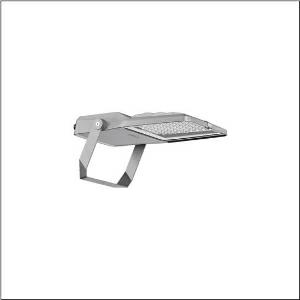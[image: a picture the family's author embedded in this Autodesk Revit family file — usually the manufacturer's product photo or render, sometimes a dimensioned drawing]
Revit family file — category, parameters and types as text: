
# Revit family: floodlight_fl_21_iq_mini___pl52_5xa7772c4d1a_fae4
name_source: partatom
category: Lighting Fixtures
units: mm (PartAtom-declared; Revit-internal decimal feet)

## family parameters
Cut with Voids When Loaded = No
Host = Face
Light Source = No
Part Type = Normal
Room Calculation Point = No
Round Connector Dimension = Use Diameter
Shared = No

## types (1)
- --- (1 x LED, 12720 lm, 87.2 W, 4000K)
    Apparent Load = 87 VA
    CIE Flux Codes = 26 60 98 100 100
    Color Rendering = 70
    Color Temperature = 4000K
    Default Elevation = 1800 mm
    Description = Floodlight FL 21 iQ mini, floodlight, primary light control with lens, of PMMA, primary optical cover: protective disc, of toughened safety glass, transparent, light distribution: PL52, light emission: direct distribution, installation type: surface-mounted, lamps: LED, High Power LED, rated values: 12.720lm | 87,2W | 145,9lm/W (begin service life); end service life: 12.720lm | 92,1W; at 50% lumin. flux: 6.360lm | 40,2W | 158,2lm/W, colour temperature: 4000K, colour rendering: CRI > 70, light colour: 740, light setting 1 begin service life: 100% | 12.720lm | 87,2W | 145,9lm/W | 4.000K, light setting 1 end service life: 92,1W, further light settings possible, control: Street-Remote, Auto-Match, Temp-Guard, Night-Set, Smart-Wire, Desk-Remote (wireless, voltage-free reading and setting of iQ features in the workshop via application-optimized NFC function/RFID function), optimised constant luminous flux control (CLO 2.0), pre-setting: linear dimming characteristic, with terminal, 6-pole, mains connection: 220..240V, AC, 50/60Hz, luminaire housing, of diecast aluminium, powder-coated, SITECO metallic grey (DB 702S), corrosivity category C5 mid according to DIN EN ISO 12944suitable for swimming poolschlorine-resistant, sealing non-destructively replaceable, mounting bracket, of steel, galvanised, powder-coated, SITECO metallic grey (DB 702S), protection rating (complete): IP66, insulation class (complete): insulation class II (safety insulation), certification: CE, ENEC, VDE, protection symbol: D, impact resistance: IK08, permissible operating ambient temperature: -40..+40°C, permissible operating ambient temperature for outdoor applications: -40..+50°C, standard: DIN EN 12944, LABS conformity tested according to VDMA 24364:2018-05, packaging unit: 1 piece

Light Distribution: PL52
    Height = 70 mm
    Lamp = 1 x LED
    Lamp Light Flux = 12720 lm
    Lamp Power = 87.2 W
    Lamp count = 1
    Length = 485 mm
    Luminous efficacy = 146 lm/W
    Manufacturer = Siteco
    ModVariant = No
    Model = 5XA7772C4D1A
    Number of Poles = 1
    OnlyDefault = Yes
    Power Factor = 1
    Product Name = Floodlight FL 21 iQ mini | PL52
    Product group = floodlight | pylon annexe
    ProductGroupID = 6201
    Protection Class = Protection class II
    Protection Degree = IP 66
    RLX_Detail_Level = 1
    RLX_Emergency_Light_Flux = 0 lm
    RLX_Emergency_Type = 0
    RLX_Emergency_Type_DB = No
    RlxData = <blob elided: 96805 chars, md5=f06a925e>
    Socket = socket
    Standby Power = 0 W
    System Light Flux = 12720 lm
    System Power = 87 W
    Type Comments = factory setting: luminous flux: 100 % | dim-lin: 254 | 456 mA
    Type Image = l_1006845.jpg
    URL = http://relux.com
    VarID = @adj_163701
    Voltage = 0 V
    Weight = 0.00 kg
    Width = 337 mm

## geometry (parser evidence)
native form markers: Blend x4, Sweep x12
no freeform markers — native parametric forms only
